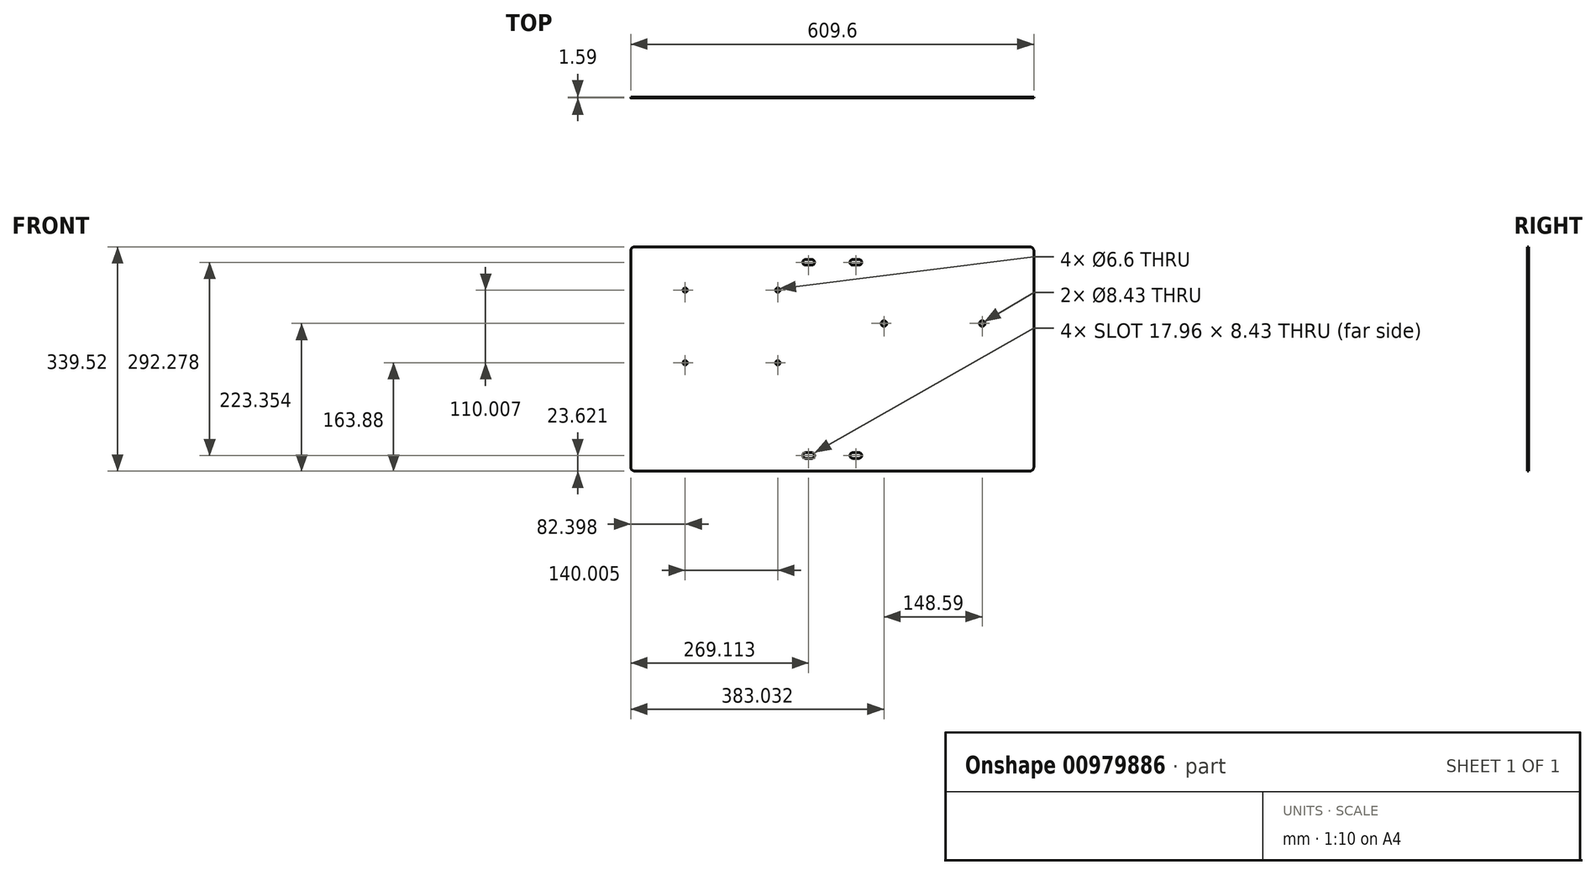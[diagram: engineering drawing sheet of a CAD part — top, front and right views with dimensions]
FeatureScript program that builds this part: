
annotation { "Feature Type Name" : "Feature", "Feature Type Description" : "" }
export const myFeature = defineFeature(function(context is Context, id is Id, definition is map)
    precondition{}
    {
        {
            var Q0;
            Q0=qCreatedBy(makeId("Front.planeOp"),FACE);
            var sketch = newSketch(context, id + "F0", { "sketchPlane" : qUnion([Q0])});
            skLineSegment(sketch, "E0.bottom", {"start": v(298.45, 169.76) * mm, "end": v(-298.45, 169.76) * mm});
            skLineSegment(sketch, "E0.top", {"start": v(298.45, -169.76) * mm, "end": v(-298.45, -169.76) * mm});
            skLineSegment(sketch, "E0.left", {"start": v(304.8, 163.41) * mm, "end": v(304.8, -163.41) * mm});
            skLineSegment(sketch, "E0.right", {"start": v(-304.8, 163.41) * mm, "end": v(-304.8, -163.41) * mm});
            skPoint(sketch, "E0.middle", {"position": v(0, 0) * mm});
            skPoint(sketch, "E1.visualSharp", {"position": v(-304.8, 169.76) * mm});
            skArc(sketch, "E1.filletArc", {"start": v(-298.45, 169.76) * mm, "mid": v(-302.94, 167.9) * mm, "end": v(-304.8, 163.41) * mm});
            skPoint(sketch, "E2.visualSharp", {"position": v(-304.8, -169.76) * mm});
            skArc(sketch, "E2.filletArc", {"start": v(-304.8, -163.41) * mm, "mid": v(-302.94, -167.9) * mm, "end": v(-298.45, -169.76) * mm});
            skPoint(sketch, "E3.visualSharp", {"position": v(304.8, 169.76) * mm});
            skArc(sketch, "E3.filletArc", {"start": v(304.8, 163.41) * mm, "mid": v(302.94, 167.9) * mm, "end": v(298.45, 169.76) * mm});
            skPoint(sketch, "E4.visualSharp", {"position": v(304.8, -169.76) * mm});
            skArc(sketch, "E4.filletArc", {"start": v(298.45, -169.76) * mm, "mid": v(302.94, -167.9) * mm, "end": v(304.8, -163.41) * mm});
            skLineSegment(sketch, "E5", {"start": v(-40.45, -146.14) * mm, "end": v(-30.92, -146.14) * mm, "construction": true});
            skLineSegment(sketch, "E6", {"start": v(30.92, -146.14) * mm, "end": v(40.45, -146.14) * mm, "construction": true});
            skPoint(sketch, "E7", {"position": v(-35.69, -146.14) * mm});
            skPoint(sketch, "E8", {"position": v(35.69, -146.14) * mm});
            skLineSegment(sketch, "E9", {"start": v(-40.45, 146.14) * mm, "end": v(-30.92, 146.14) * mm, "construction": true});
            skLineSegment(sketch, "E10", {"start": v(30.92, 146.14) * mm, "end": v(40.45, 146.14) * mm, "construction": true});
            skPoint(sketch, "E11", {"position": v(-35.69, 146.14) * mm});
            skPoint(sketch, "E12", {"position": v(35.69, 146.14) * mm});
            skArc(sketch, "E13.0.startCap", {"start": v(-40.45, 141.92) * mm, "mid": v(-44.67, 146.14) * mm, "end": v(-40.45, 150.36) * mm});
            skArc(sketch, "E13.0.endCap", {"start": v(-30.92, 150.36) * mm, "mid": v(-26.7, 146.14) * mm, "end": v(-30.92, 141.92) * mm});
            skLineSegment(sketch, "E13.0.left", {"start": v(-40.45, 150.36) * mm, "end": v(-30.92, 150.36) * mm});
            skLineSegment(sketch, "E13.0.right", {"start": v(-40.45, 141.92) * mm, "end": v(-30.92, 141.92) * mm});
            skArc(sketch, "E13.1.startCap", {"start": v(30.92, 141.92) * mm, "mid": v(26.7, 146.14) * mm, "end": v(30.92, 150.36) * mm});
            skArc(sketch, "E13.1.endCap", {"start": v(40.45, 150.36) * mm, "mid": v(44.67, 146.14) * mm, "end": v(40.45, 141.92) * mm});
            skLineSegment(sketch, "E13.1.left", {"start": v(30.92, 150.36) * mm, "end": v(40.45, 150.36) * mm});
            skLineSegment(sketch, "E13.1.right", {"start": v(30.92, 141.92) * mm, "end": v(40.45, 141.92) * mm});
            skArc(sketch, "E13.2.startCap", {"start": v(-40.45, -150.36) * mm, "mid": v(-44.67, -146.14) * mm, "end": v(-40.45, -141.92) * mm});
            skArc(sketch, "E13.2.endCap", {"start": v(-30.92, -141.92) * mm, "mid": v(-26.7, -146.14) * mm, "end": v(-30.92, -150.36) * mm});
            skLineSegment(sketch, "E13.2.left", {"start": v(-40.45, -141.92) * mm, "end": v(-30.92, -141.92) * mm});
            skLineSegment(sketch, "E13.2.right", {"start": v(-40.45, -150.36) * mm, "end": v(-30.92, -150.36) * mm});
            skArc(sketch, "E13.3.startCap", {"start": v(30.92, -150.36) * mm, "mid": v(26.7, -146.14) * mm, "end": v(30.92, -141.92) * mm});
            skArc(sketch, "E13.3.endCap", {"start": v(40.45, -141.92) * mm, "mid": v(44.67, -146.14) * mm, "end": v(40.45, -150.36) * mm});
            skLineSegment(sketch, "E13.3.left", {"start": v(30.92, -141.92) * mm, "end": v(40.45, -141.92) * mm});
            skLineSegment(sketch, "E13.3.right", {"start": v(30.92, -150.36) * mm, "end": v(40.45, -150.36) * mm});
            skLineSegment(sketch, "E14.bottom", {"start": v(-82.4, 104.13) * mm, "end": v(-222.4, 104.13) * mm, "construction": true});
            skLineSegment(sketch, "E14.top", {"start": v(-82.4, -5.88) * mm, "end": v(-222.4, -5.88) * mm, "construction": true});
            skLineSegment(sketch, "E14.left", {"start": v(-82.4, 104.13) * mm, "end": v(-82.4, -5.88) * mm, "construction": true});
            skLineSegment(sketch, "E14.right", {"start": v(-222.4, 104.13) * mm, "end": v(-222.4, -5.88) * mm, "construction": true});
            skPoint(sketch, "E14.middle", {"position": v(-152.4, 49.12) * mm});
            skLineSegment(sketch, "E15", {"start": v(78.23, 53.6) * mm, "end": v(226.82, 53.6) * mm, "construction": true});
            skCircle(sketch, "E16", {"center": v(-222.4, 104.13) * mm, "radius": 3.3 * mm});
            skCircle(sketch, "E17", {"center": v(-82.4, 104.13) * mm, "radius": 3.3 * mm});
            skCircle(sketch, "E18", {"center": v(-222.4, -5.88) * mm, "radius": 3.3 * mm});
            skCircle(sketch, "E19", {"center": v(-82.4, -5.88) * mm, "radius": 3.3 * mm});
            skCircle(sketch, "E20", {"center": v(78.23, 53.6) * mm, "radius": 4.22 * mm});
            skCircle(sketch, "E21", {"center": v(226.82, 53.6) * mm, "radius": 4.22 * mm});
            skSolve(sketch);
        }
        {
            var Q0;
            Q0=qSketchRegion(id+"F0",true);
            extrude(context, id + "F1", {"entities" : qUnion([Q0]), "depth" : 1.59 * mm, "offsetDistance" : 25.4 * mm});
        }
    });
